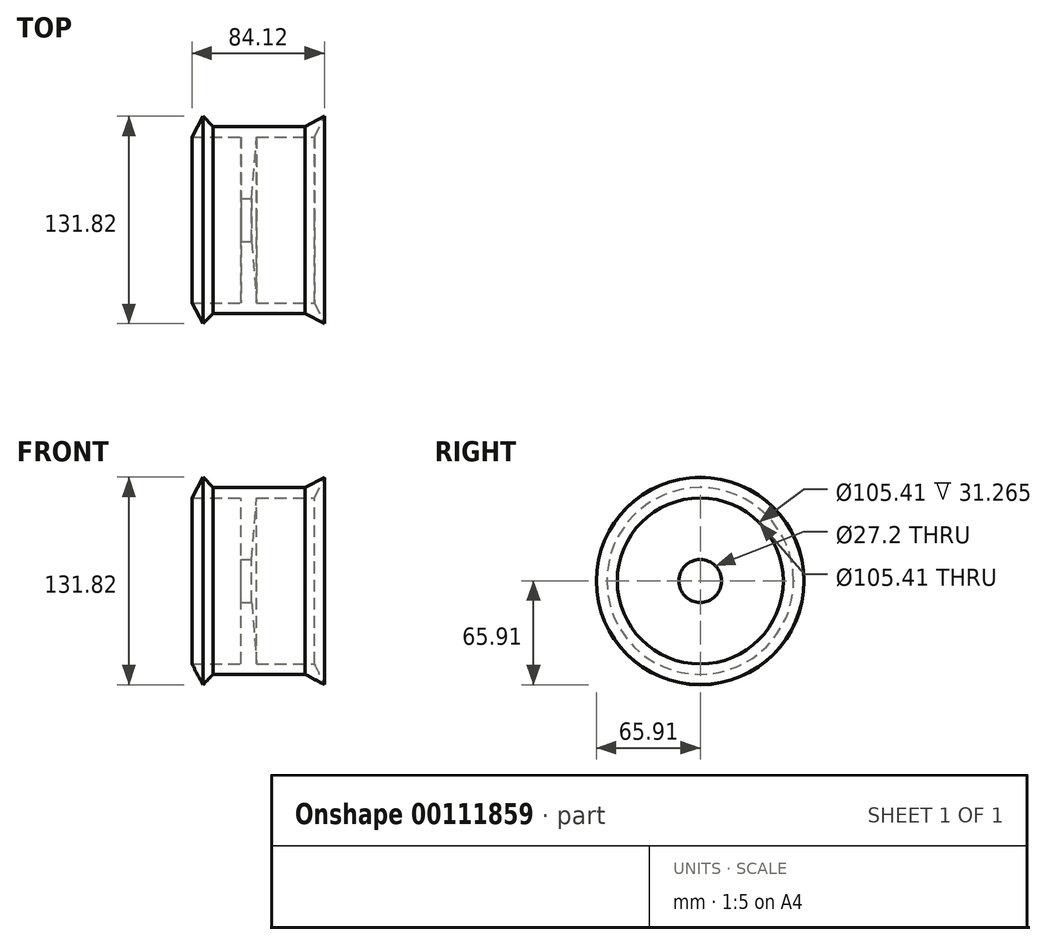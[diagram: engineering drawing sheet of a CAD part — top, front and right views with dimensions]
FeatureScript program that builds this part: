
annotation { "Feature Type Name" : "Feature", "Feature Type Description" : "" }
export const myFeature = defineFeature(function(context is Context, id is Id, definition is map)
    precondition{}
    {
        {
            var Q0;
            Q0=qCreatedBy(makeId("Front.planeOp"),FACE);
            var sketch = newSketch(context, id + "F0", { "sketchPlane" : qUnion([Q0])});
            skLineSegment(sketch, "E0", {"start": v(-41.13, 52.7) * mm, "end": v(-9.86, 52.7) * mm});
            skLineSegment(sketch, "E1", {"start": v(36.66, 52.7) * mm, "end": v(42.99, 65.82) * mm});
            skLineSegment(sketch, "E2", {"start": v(42.99, 65.82) * mm, "end": v(30.7, 59.3) * mm});
            skLineSegment(sketch, "E3", {"start": v(30.7, 59.3) * mm, "end": v(-27.73, 59.3) * mm});
            skLineSegment(sketch, "E4", {"start": v(-27.73, 59.3) * mm, "end": v(-34.06, 65.91) * mm});
            skLineSegment(sketch, "E5", {"start": v(-34.06, 65.91) * mm, "end": v(-41.13, 52.7) * mm});
            skLineSegment(sketch, "E6", {"start": v(-9.86, 52.7) * mm, "end": v(-9.86, 13.6) * mm});
            skLineSegment(sketch, "E7", {"start": v(-9.86, 13.6) * mm, "end": v(-3.16, 13.6) * mm});
            skLineSegment(sketch, "E8", {"start": v(-3.16, 13.6) * mm, "end": v(0, 52.7) * mm});
            skLineSegment(sketch, "E9.trimOffspring", {"start": v(0, 52.7) * mm, "end": v(36.66, 52.7) * mm});
            skLineSegment(sketch, "E10", {"start": v(0, 0) * mm, "end": v(-52.26, 0) * mm, "construction": true});
            skSolve(sketch);
        }
        {
            var Q0;
            Q0=makeQuery(id+"F0.imprint","IMPRINT",FACE,{"disambiguationData":[TD([[makeQuery(id+"F0.imprint","IMPRINT",EDGE,{"derivedFrom":sQuery(id+"F0.wireOp",EDGE,"E0")}),1.0]])]});
            var Q1;
            Q1=sQuery(id+"F0.wireOp",EDGE,"E10");
            revolve(context, id + "F1", {"entities" : qUnion([Q0]), "axis" : qUnion([Q1]), "revolveType" : RevolveType.FULL});
        }
    });
